# Revit family: 3-537-xx - 37-537-xx - Adelphi (Vanity)
name_source: partatom
category: Lighting Fixtures
units: mm (PartAtom-declared; Revit-internal decimal feet)

## family parameters
Cut with Voids When Loaded = No
Host = Face
Light Source = Yes
Part Type = Normal
Room Calculation Point = No
Round Connector Dimension = Use Diameter
Shared = No

## types (6) — shared parameters
Color Filter = 16777215
Dimming Lamp Color Temperature Shift = <None>
Emit Shape Visible in Rendering = No
Emit from Rectangle Length = 1 "
Emit from Rectangle Width = 22 "
Lamp = LED Array
Main Diffuser = Matte White Acrylic
Manufacturer = Oxygen - Lighting & Fans
Model = 3-555-xx - 37-555-xx - Adelphi Vanity
Photometric Web File = 3-537 Adelphi Vanity.ies
Tilt Angle = 0.00°
URL = www.oxygenlighting.com
Wattage Comments = 15.00W at 120 V
zero-valued in all types: Default Elevation

## per-type parameters (varying)
| type | Metal Finish | Voltage |
| 3-555-24 / Satin Nickel - Matte White Acrylic | 24 - Satin Nickel | 120 V |
| 3-555-22 / Oiled Bronze - Matte White Acrylic | 22- Oiled Bronze | 120 V |
| 3-555-40 / Aged Brass - Matte White Acrylic | 40 - Aged Brass | 120 V |
| 37-555-22 / Oiled Bronze - Matte White Acrylic | 22- Oiled Bronze | 277 V |
| 37-555-24 / Satin Nickel - Matte White Acrylic | 24 - Satin Nickel | 277 V |
| 37-555-40 / Aged Brass - Matte White Acrylic | 40 - Aged Brass | 277 V |

## geometry (parser evidence)
native form markers: Sweep x5
no freeform markers — native parametric forms only
